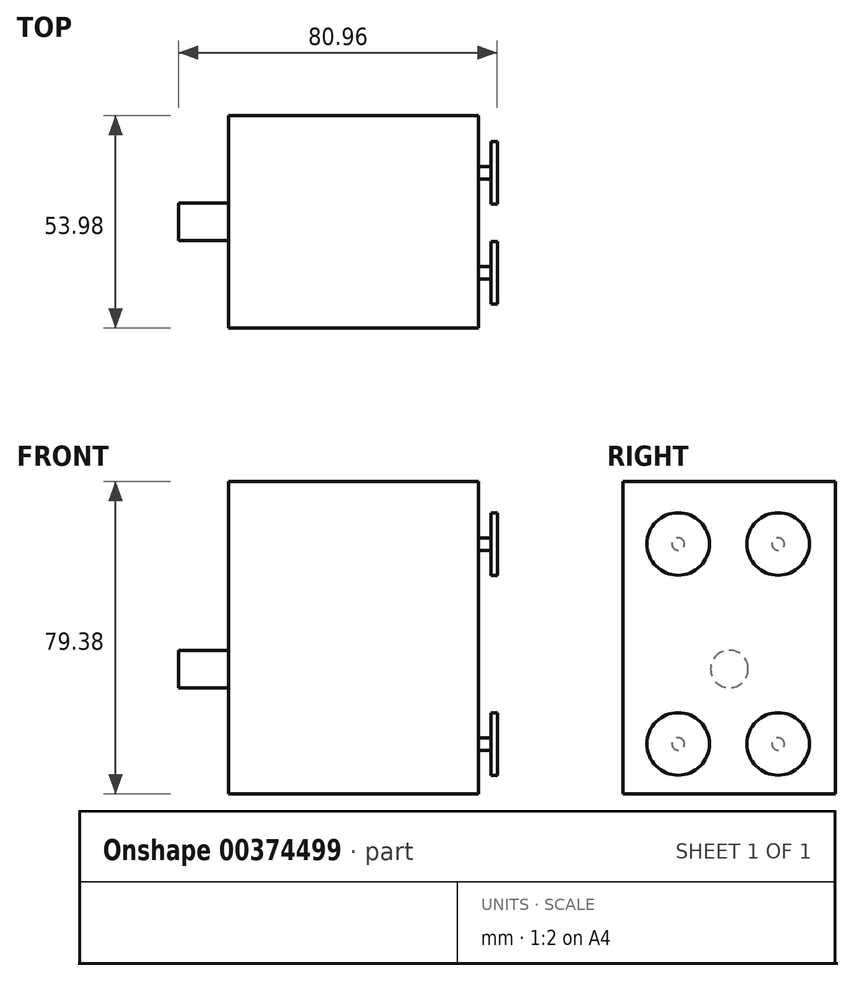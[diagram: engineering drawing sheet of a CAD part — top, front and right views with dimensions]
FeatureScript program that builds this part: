
annotation { "Feature Type Name" : "Feature", "Feature Type Description" : "" }
export const myFeature = defineFeature(function(context is Context, id is Id, definition is map)
    precondition{}
    {
        {
            var Q0;
            Q0=qCreatedBy(makeId("Front.planeOp"),FACE);
            var sketch = newSketch(context, id + "F0", { "sketchPlane" : qUnion([Q0])});
            skLineSegment(sketch, "E0.bottom", {"start": v(-31.75, 39.69) * mm, "end": v(31.75, 39.69) * mm});
            skLineSegment(sketch, "E0.top", {"start": v(-31.75, -39.69) * mm, "end": v(31.75, -39.69) * mm});
            skLineSegment(sketch, "E0.left", {"start": v(-31.75, 39.69) * mm, "end": v(-31.75, -39.69) * mm});
            skLineSegment(sketch, "E0.right", {"start": v(31.75, 39.69) * mm, "end": v(31.75, -39.69) * mm});
            skPoint(sketch, "E0.middle", {"position": v(0, 0) * mm});
            skSolve(sketch);
        }
        {
            var Q0;
            Q0 = qSketchRegion(id + "F0", true);
            extrude(context, id + "F1", {"entities" : qUnion([Q0]), "depth" : 53.97 * mm});
        }
        {
            var Q0;
            Q0=makeQuery(id+"F1.opExtrude","SWEPT_FACE",FACE,{"disambiguationData":[OSD([sQuery(id+"F0.wireOp",EDGE,"E0.right")])]});
            var sketch = newSketch(context, id + "F2", { "sketchPlane" : qUnion([Q0])});
            skCircle(sketch, "E1", {"center": v(-40, 23.81) * mm, "radius": 1.59 * mm});
            skCircle(sketch, "E2.0.1.0", {"center": v(-40, -26.99) * mm, "radius": 1.59 * mm});
            skCircle(sketch, "E2.1.0.0", {"center": v(-14.6, 23.81) * mm, "radius": 1.59 * mm});
            skCircle(sketch, "E2.1.1.0", {"center": v(-14.6, -26.99) * mm, "radius": 1.59 * mm});
            skLineSegment(sketch, "E2.direction1", {"start": v(-40, 23.81) * mm, "end": v(-14.6, 23.81) * mm, "construction": true});
            skLineSegment(sketch, "E2.direction2", {"start": v(-40, 23.81) * mm, "end": v(-40, -26.99) * mm, "construction": true});
            skSolve(sketch);
        }
        {
            var Q0;
            Q0 = qSketchRegion(id + "F2", true);
            extrude(context, id + "F3", {"entities" : qUnion([Q0]), "operationType" : NewBodyOperationType.ADD, "depth" : 3.17 * mm});
        }
        {
            var Q0;
            Q0=makeQuery(id+"F3.opExtrude","CAP_FACE",FACE,{"disambiguationData":[OSD([sQuery(id+"F2.wireOp",EDGE,"E1")])],"isStart":false});
            var sketch = newSketch(context, id + "F4", { "sketchPlane" : qUnion([Q0])});
            skCircle(sketch, "E3", {"center": v(-40, 23.81) * mm, "radius": 7.94 * mm});
            skCircle(sketch, "E4", {"center": v(-14.6, 23.81) * mm, "radius": 7.94 * mm});
            skCircle(sketch, "E5", {"center": v(-40, -26.99) * mm, "radius": 7.94 * mm});
            skCircle(sketch, "E6", {"center": v(-14.6, -26.99) * mm, "radius": 7.94 * mm});
            skSolve(sketch);
        }
        {
            var Q0;
            Q0 = qSketchRegion(id + "F4", true);
            extrude(context, id + "F5", {"entities" : qUnion([Q0]), "operationType" : NewBodyOperationType.ADD, "depth" : 1.59 * mm});
        }
        {
            var Q0;
            Q0=makeQuery(id+"F1.opExtrude","SWEPT_FACE",FACE,{"disambiguationData":[OSD([sQuery(id+"F0.wireOp",EDGE,"E0.left")])]});
            var sketch = newSketch(context, id + "F6", { "sketchPlane" : qUnion([Q0])});
            skCircle(sketch, "E7", {"center": v(26.99, -7.94) * mm, "radius": 4.76 * mm});
            skSolve(sketch);
        }
        {
            var Q0;
            Q0 = qSketchRegion(id + "F6", true);
            extrude(context, id + "F7", {"entities" : qUnion([Q0]), "operationType" : NewBodyOperationType.ADD, "depth" : 12.7 * mm});
        }
    });
